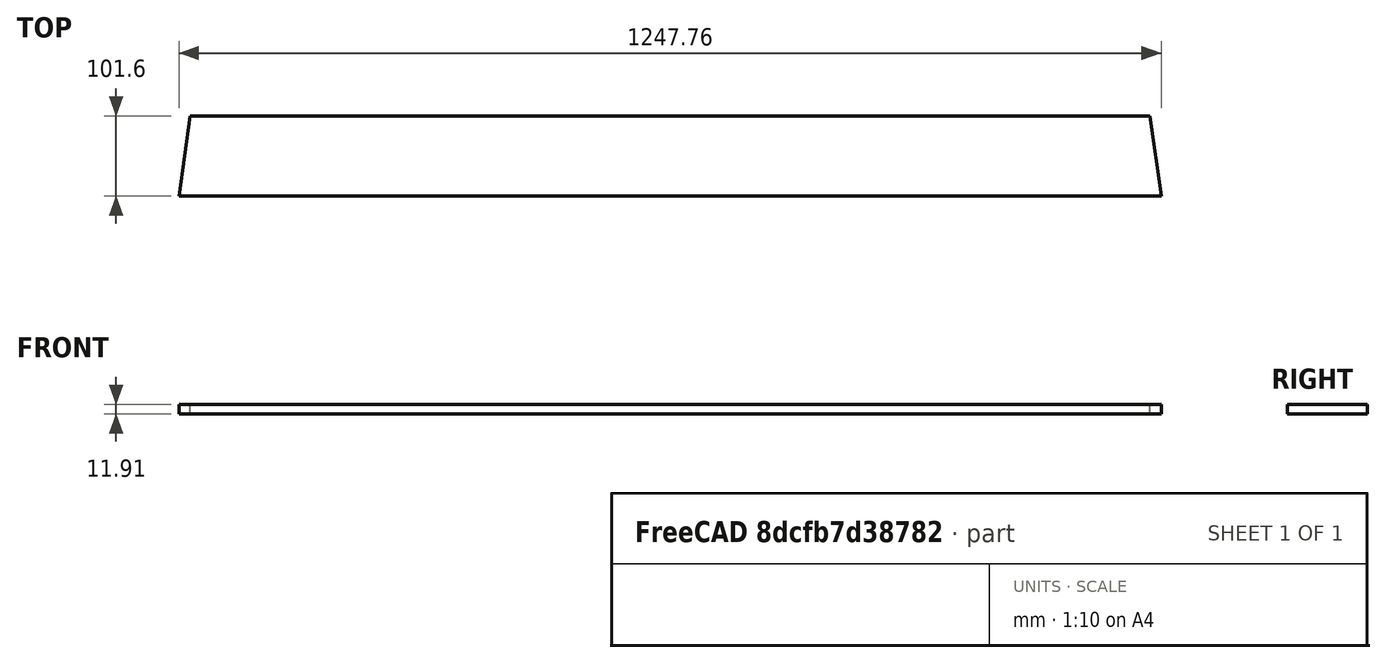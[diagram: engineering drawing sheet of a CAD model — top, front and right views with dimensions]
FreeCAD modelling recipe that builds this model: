
FCSTD DOCUMENT  (FreeCAD 0.20R29603 (Git))
Label: LongSkirt
License: All rights reserved
LicenseURL: http://en.wikipedia.org/wiki/All_rights_reserved
objects: App::DocumentObjectGroup×3, Sketcher::SketchObject×1, PartDesign::Pad×1, PartDesign::Body×1, PartDesign::CoordinateSystem×1, App::FeaturePython×1, App::Part×1
note: 5 computed .brp shape members not serialized (recipe doc carries the construction recipe); baked Part::Feature solids carry a one-line shape summary decoded from their .brp
EXTERNAL_REF file=Parameters.FCStd obj=Spreadsheet

FEATURE [Sketcher::SketchObject] Sketch
  FullyConstrained = true
  MapMode = 5
  Support = -> [XY_Plane]
  expr: Constraints[17] = <<Parameters>>#<<DeskDimensions>>.Skirt_Length
  expr: Constraints[18] = <<Parameters>>#<<DeskDimensions>>.Skirt_Height
  expr: Constraints[3] = Parameters#<<DeskDimensions>>.Skirt_Length
  sketch-geometry (8):
    g0: LineSegment StartX=-609.6 StartY=0 StartZ=0 EndX=609.6 EndY=0 EndZ=0
    g1: LineSegment StartX=609.6 StartY=0 StartZ=0 EndX=623.879 EndY=-101.6 EndZ=0
    g2: LineSegment StartX=-623.879 StartY=-101.6 StartZ=0 EndX=-609.6 EndY=0 EndZ=0
    g3: LineSegment StartX=-623.879 StartY=-101.6 StartZ=0 EndX=623.879 EndY=-101.6 EndZ=0
    g4: LineSegment StartX=-609.6 StartY=0 StartZ=0 EndX=609.6 EndY=0 EndZ=0
    g5: LineSegment StartX=609.6 StartY=0 StartZ=0 EndX=609.6 EndY=-101.6 EndZ=0
    g6: LineSegment StartX=609.6 StartY=-101.6 StartZ=0 EndX=-609.6 EndY=-101.6 EndZ=0
    g7: LineSegment StartX=-609.6 StartY=-101.6 StartZ=0 EndX=-609.6 EndY=0 EndZ=0
  constraints (22):
    c: Coincident(g0,g1)
    c: Coincident(g2,g0)
    c: Horizontal(g0)
    c: DistanceX(g0,g0) = 1219.2
    c: Angle(g2,g0) = 1.71042
    c: Angle(g0,g1) = 1.71042
    c: Coincident(g3,g2)
    c: Coincident(g3,g1)
    c: Horizontal(g3)
    c: Coincident(g4,g5)
    c: Coincident(g5,g6)
    c: Coincident(g6,g7)
    c: Coincident(g7,g4)
    c: Horizontal(g4)
    c: Horizontal(g6)
    c: Vertical(g5)
    c: Vertical(g7)
    c: DistanceX(g4,g4) = 1219.2
    c: DistanceY(g5,g5) = 101.6
    c: Coincident(g0,g4)
    c: PointOnObject(g6,g3)
    c: Symmetric(g0,g0,g-1)
FEATURE [PartDesign::Pad] Pad
  Direction = (0,0,1)
  Length = 11.9062
  Length2 = 10
  Profile = -> Sketch
  ReferenceAxis = -> Sketch [N_Axis]
  Type = 0
  expr: Length = Parameters#<<DeskDimensions>>.Stock_Thickness
FEATURE [PartDesign::Body] Body
  Group = -> [Sketch,Pad]
  Origin = -> Origin
  Tip = -> Pad
FEATURE [App::DocumentObjectGroup] Parts
FEATURE [PartDesign::CoordinateSystem] LCS_Origin
  AttacherType = Attacher::AttachEngine3D
  MapMode = 2
  Support = -> [X_Axis001]
FEATURE [App::DocumentObjectGroup] Constraints
FEATURE [App::FeaturePython] Variables  # WARN: FeaturePython — macro-defined, semantics opaque (R4)
  Type = App::PropertyContainer
FEATURE [App::DocumentObjectGroup] Configurations
FEATURE [App::Part] Model
  Group = -> [LCS_Origin,Constraints,Variables,Configurations,Body]
  Origin = -> Origin001
  Type = Assembly
